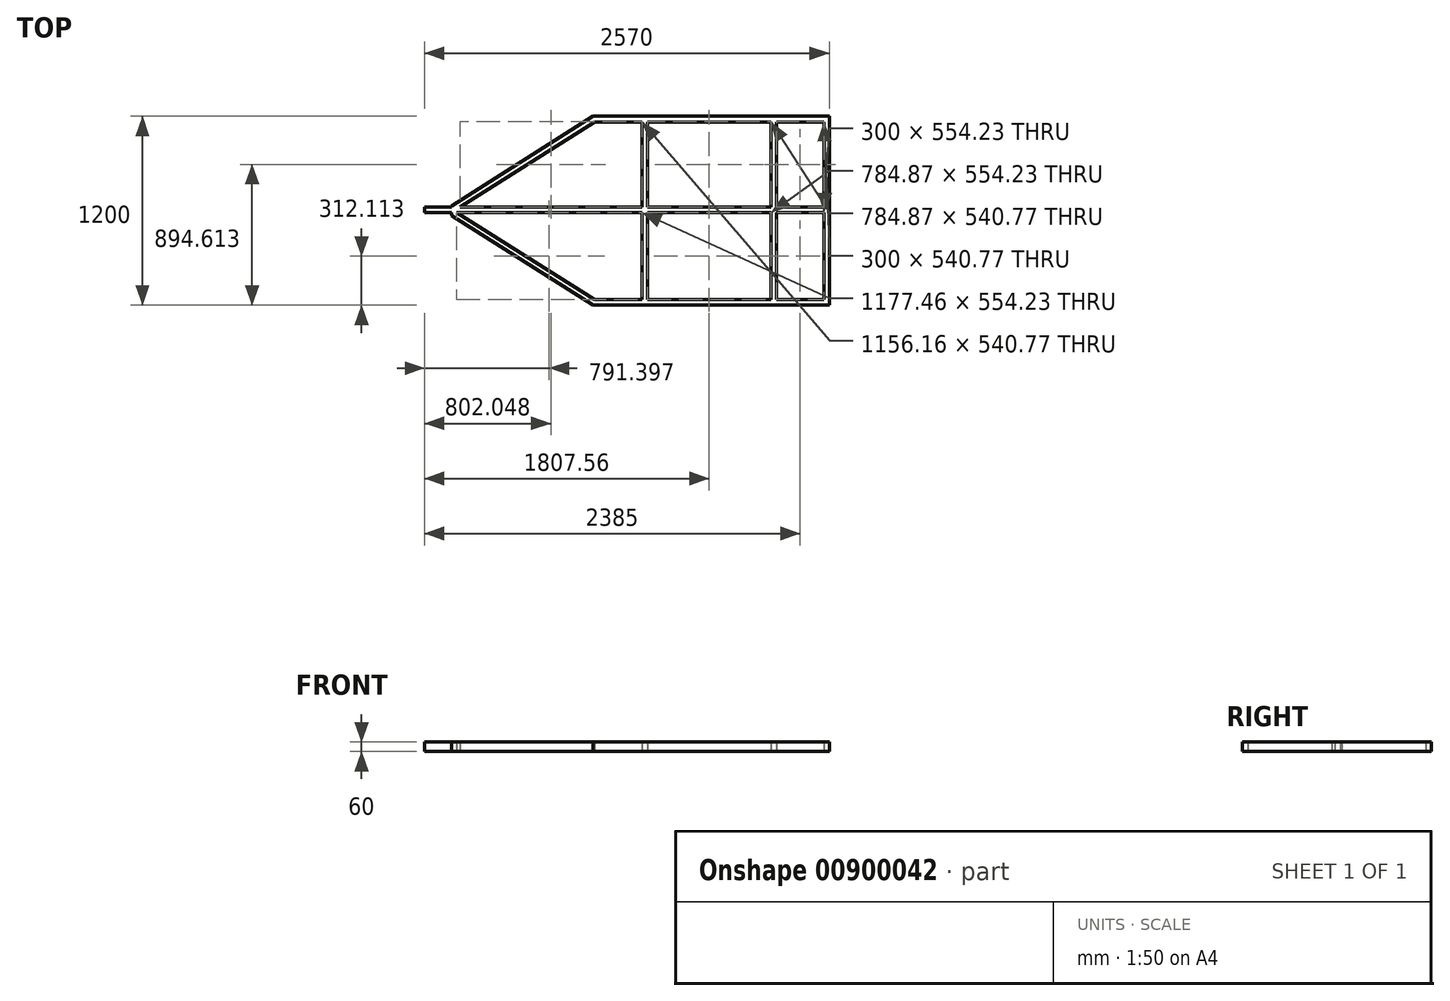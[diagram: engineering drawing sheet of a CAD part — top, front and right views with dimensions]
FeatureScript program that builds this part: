
annotation { "Feature Type Name" : "Feature", "Feature Type Description" : "" }
export const myFeature = defineFeature(function(context is Context, id is Id, definition is map)
    precondition{}
    {
        {
            var Q0;
            Q0=qCreatedBy(makeId("Top.planeOp"),FACE);
            var sketch = newSketch(context, id + "F0", { "sketchPlane" : qUnion([Q0])});
            skLineSegment(sketch, "E0", {"start": v(1186.37, 598.9) * mm, "end": v(1186.37, -601.1) * mm});
            skLineSegment(sketch, "E1", {"start": v(1186.37, -601.1) * mm, "end": v(-313.63, -601.1) * mm});
            skLineSegment(sketch, "E2", {"start": v(-313.63, -601.1) * mm, "end": v(-1213.63, -32.62) * mm});
            skLineSegment(sketch, "E3", {"start": v(-1213.63, -32.62) * mm, "end": v(-1213.63, -11.86) * mm});
            skLineSegment(sketch, "E4", {"start": v(-1213.63, 30.44) * mm, "end": v(-313.63, 598.9) * mm});
            skLineSegment(sketch, "E5", {"start": v(-313.63, 598.9) * mm, "end": v(1186.37, 598.9) * mm});
            skLineSegment(sketch, "E6.1", {"start": v(-303.5, 563.9) * mm, "end": v(-3.5, 563.9) * mm});
            skLineSegment(sketch, "E6.2", {"start": v(1151.37, 563.9) * mm, "end": v(1151.37, 23.14) * mm});
            skLineSegment(sketch, "E6.3", {"start": v(-1159.66, 23.14) * mm, "end": v(-303.5, 563.9) * mm});
            skLineSegment(sketch, "E6.4", {"start": v(1151.37, -566.1) * mm, "end": v(851.37, -566.1) * mm});
            skLineSegment(sketch, "E6.5", {"start": v(-303.5, -566.1) * mm, "end": v(-1180.96, -11.86) * mm});
            skLineSegment(sketch, "E7", {"start": v(851.37, 563.9) * mm, "end": v(851.37, 23.14) * mm});
            skLineSegment(sketch, "E8", {"start": v(816.37, -566.1) * mm, "end": v(816.37, -11.86) * mm});
            skLineSegment(sketch, "E9", {"start": v(-3.5, 563.9) * mm, "end": v(-3.5, 23.14) * mm});
            skLineSegment(sketch, "E10", {"start": v(31.5, -566.1) * mm, "end": v(31.5, -11.86) * mm});
            skLineSegment(sketch, "E11.trimOffspring", {"start": v(31.5, 563.9) * mm, "end": v(816.37, 563.9) * mm});
            skLineSegment(sketch, "E12.trimOffspring", {"start": v(851.37, 563.9) * mm, "end": v(1151.37, 563.9) * mm});
            skLineSegment(sketch, "E13.trimOffspring", {"start": v(-3.5, -566.1) * mm, "end": v(-303.5, -566.1) * mm});
            skLineSegment(sketch, "E14.trimOffspring", {"start": v(816.37, -566.1) * mm, "end": v(31.5, -566.1) * mm});
            skLineSegment(sketch, "E15", {"start": v(-1159.66, 23.14) * mm, "end": v(-3.5, 23.14) * mm});
            skLineSegment(sketch, "E16", {"start": v(1151.37, -11.86) * mm, "end": v(851.37, -11.86) * mm});
            skLineSegment(sketch, "E17", {"start": v(-1213.63, -11.86) * mm, "end": v(-1383.63, -11.86) * mm});
            skLineSegment(sketch, "E18", {"start": v(-1383.63, -11.86) * mm, "end": v(-1383.63, 23.14) * mm});
            skLineSegment(sketch, "E19", {"start": v(-1383.63, 23.14) * mm, "end": v(-1213.63, 23.14) * mm});
            skLineSegment(sketch, "E20.trimOffspring", {"start": v(-1213.63, 23.14) * mm, "end": v(-1213.63, 30.44) * mm});
            skLineSegment(sketch, "E21.trimOffspring", {"start": v(31.5, 23.14) * mm, "end": v(816.37, 23.14) * mm});
            skLineSegment(sketch, "E22.trimOffspring", {"start": v(-3.5, -11.86) * mm, "end": v(-3.5, -566.1) * mm});
            skLineSegment(sketch, "E23.trimOffspring", {"start": v(31.5, 23.14) * mm, "end": v(31.5, 563.9) * mm});
            skLineSegment(sketch, "E24.trimOffspring", {"start": v(-3.5, -11.86) * mm, "end": v(-1180.96, -11.86) * mm});
            skLineSegment(sketch, "E25.trimOffspring", {"start": v(851.37, 23.14) * mm, "end": v(1151.37, 23.14) * mm});
            skLineSegment(sketch, "E26.trimOffspring", {"start": v(816.37, 23.14) * mm, "end": v(816.37, 563.9) * mm});
            skLineSegment(sketch, "E27.trimOffspring", {"start": v(816.37, -11.86) * mm, "end": v(31.5, -11.86) * mm});
            skLineSegment(sketch, "E28.trimOffspring", {"start": v(851.37, -11.86) * mm, "end": v(851.37, -566.1) * mm});
            skLineSegment(sketch, "E29.trimOffspring", {"start": v(1151.37, -11.86) * mm, "end": v(1151.37, -566.1) * mm});
            skSolve(sketch);
        }
        {
            var Q0;
            Q0=makeQuery(id+"F0.imprint","IMPRINT",FACE,{"disambiguationData":[TD([[makeQuery(id+"F0.imprint","IMPRINT",EDGE,{"derivedFrom":sQuery(id+"F0.wireOp",EDGE,"E0")}),-1.0]])]});
            extrude(context, id + "F1", {"entities" : qUnion([Q0]), "depth" : 60 * mm, "offsetDistance" : 25 * mm});
        }
    });
